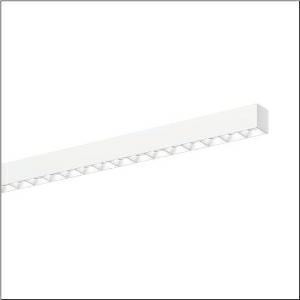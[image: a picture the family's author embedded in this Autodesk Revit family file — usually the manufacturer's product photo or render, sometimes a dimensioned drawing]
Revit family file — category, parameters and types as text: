
# Revit family: silica_21_51mx26da34wb
name_source: partatom
category: Lighting Fixtures
units: mm (PartAtom-declared; Revit-internal decimal feet)

## family parameters
Cut with Voids When Loaded = No
Host = Face
Light Source = No
Part Type = Normal
Room Calculation Point = No
Round Connector Dimension = Use Diameter
Shared = No

## types (1)
- --- (1 x LED, 4320 lm, 25.1 W, 3000K)
    Apparent Load = 25 VA
    CIE Flux Codes = 83 98 100 100 100
    Color Rendering = 80
    Color Temperature = 3000K
    Default Elevation = 1800 mm
    Description = Silica 21, office luminaire, primary light control with darklight reflector, of PMMA, white, CAT 2 (L<= 3000cd/m²), light emission: direct distribution, primary light characteristic: symmetric, installation type: surface-mounted, LED, rated luminous flux: 4.320lm, luminous efficacy: 172lm/W, light colour: 830, colour temperature: 3000K, control gear: DALI 2, with terminal, 3+2-pole, max. 2.5mm², mains connection: 220..240V, AC, 50/60Hz, rated input power: 25.1W, luminaire housing, of aluminium, traffic white (RAL 9016), length: 1.204mm, width: 53mm, height: 53mm, protection rating (complete): IP20, insulation class (complete): insulation class I (protective earthing), certification: CE, permissible operating ambient temperature: 0..+35°C, standard: EN 50419, packaging unit: 1 piece
    Height = 53 mm
    Lamp = 1 x LED
    Lamp Light Flux = 4320 lm
    Lamp Power = 25.1 W
    Lamp count = 1
    Length = 1204 mm
    Luminous efficacy = 172 lm/W
    Manufacturer = Siteco
    ModVariant = No
    Model = 51MX26DA34WB
    Mounting Place = Ceiling
    Mounting Type = Surface mounted
    Number of Poles = 1
    OnlyDefault = Yes
    Power Factor = 1
    Product Name = Silica 21
    Product group = office luminaire | ceiling mounted
    ProductGroupID = 301
    Protection Class = Protection class I
    Protection Degree = IP 20
    RLX_Detail_Level = 1
    RLX_Emergency_Light_Flux = 0 lm
    RLX_Emergency_Type = 0
    RLX_Emergency_Type_DB = No
    RlxData = <blob elided: 38301 chars, md5=330e7155>
    Socket = socket
    Standby Power = 0 W
    System Light Flux = 4320 lm
    System Power = 25 W
    Type Comments = factory setting: luminous flux: 100 % | dim-lin: 254 | 360 mA
    Type Image = l_1335934.jpg
    URL = http://relux.com
    VarID = @adj_028749
    Voltage = 0 V
    Weight = 0.00 kg
    Width = 53 mm

## geometry (parser evidence)
native form markers: Blend x4, Sweep x10
no freeform markers — native parametric forms only
